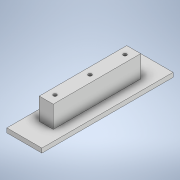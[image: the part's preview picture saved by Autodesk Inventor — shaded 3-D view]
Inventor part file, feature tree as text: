
AUTODESK INVENTOR PART (.ipt)
format: ipt  version: 2022 (Build 260153000, 153)  size: 133,632 bytes
history: native  units: in
note: dims shown in document units (in); Inventor stores cm internally (conversion verified against a paired STEP export)
features: extrude x3, sketch x3
ambient origin geometry x8: Origin, YZ Plane, XZ Plane, XY Plane, X Axis, Y Axis, Z Axis, Center Point
bodies: Solid1 (feature_tree)
feature tree (6):
  extrude  "Extrusion1"  Depth=5.9055in
  extrude  "Extrusion2"  Depth=0.1969in
  extrude  "Extrusion3"  Depth=0.4921in
  sketch  "Sketch1"  dims[d0=1.5748in d1=5.9055in]
  sketch  "Sketch2"  dims[d2=0.1969in d3=0.0in d4=2.9528in]
  sketch  "Sketch3"  dims[d5=1.5748in d6=0.315in d7=0.3937in d8=0.315in d9=1.5748in d10=0.3937in d11=0.9843in d12=0.0in d13=1.5748in d14=3.1496in d15=0.1575in d16=0.1575in d17=0.1575in d18=0.4921in d19=0.0in d20=0.0197in d21=0.0344in]
